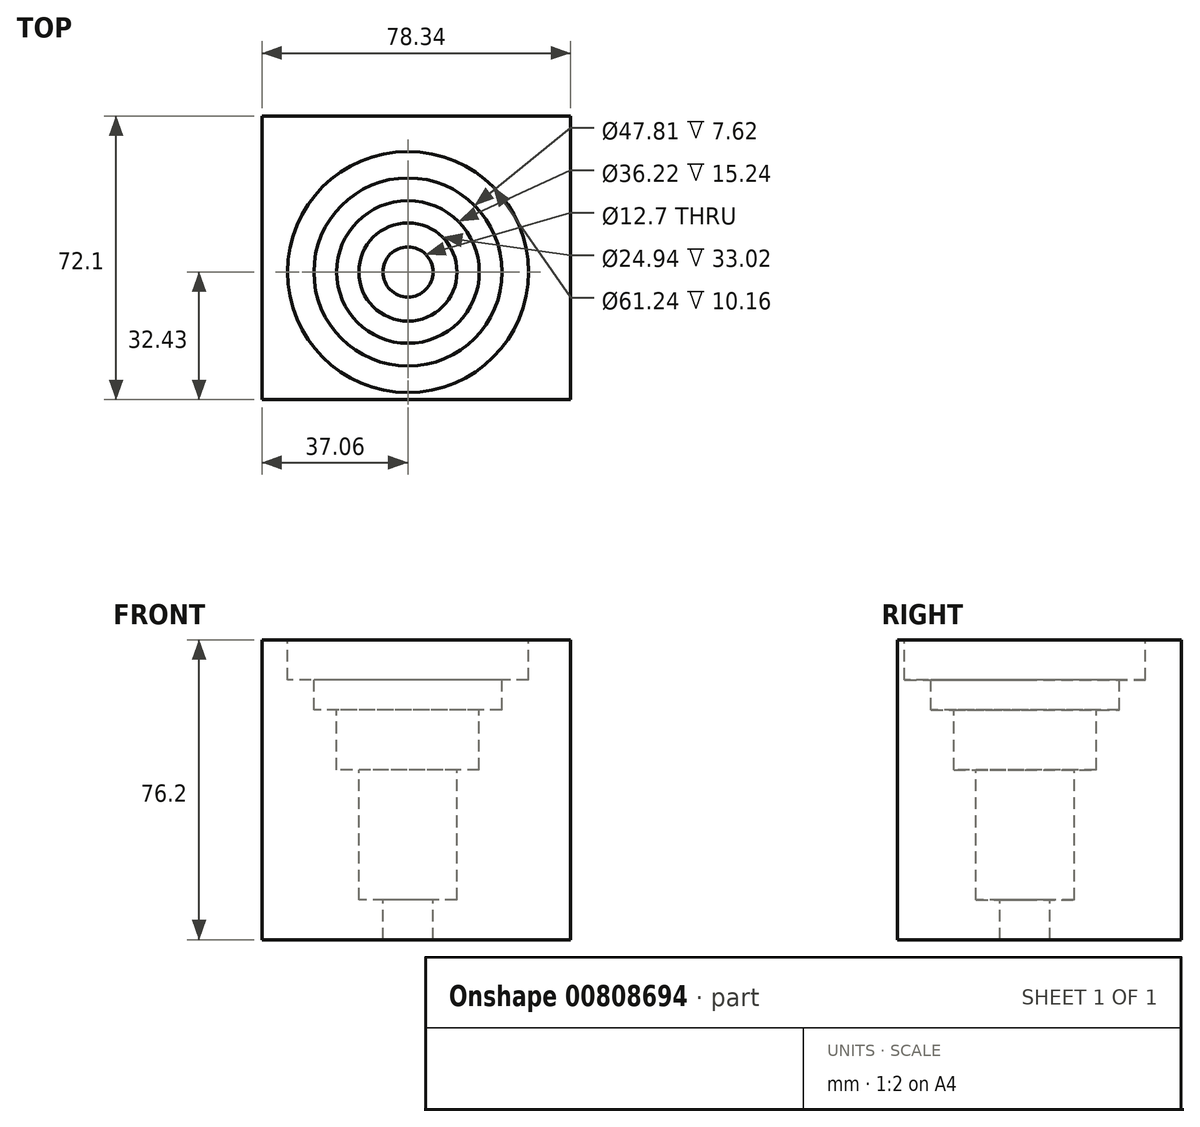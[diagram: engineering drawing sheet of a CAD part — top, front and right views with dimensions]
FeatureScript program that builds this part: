
annotation { "Feature Type Name" : "Feature", "Feature Type Description" : "" }
export const myFeature = defineFeature(function(context is Context, id is Id, definition is map)
    precondition{}
    {
        {
            var Q0;
            Q0=qCreatedBy(makeId("Top.planeOp"),FACE);
            var sketch = newSketch(context, id + "F0", { "sketchPlane" : qUnion([Q0])});
            skLineSegment(sketch, "E0.bottom", {"start": v(-37.06, -32.43) * mm, "end": v(41.28, -32.43) * mm});
            skLineSegment(sketch, "E0.top", {"start": v(-37.06, 39.67) * mm, "end": v(41.28, 39.67) * mm});
            skLineSegment(sketch, "E0.left", {"start": v(-37.06, -32.43) * mm, "end": v(-37.06, 39.67) * mm});
            skLineSegment(sketch, "E0.right", {"start": v(41.28, -32.43) * mm, "end": v(41.28, 39.67) * mm});
            skSolve(sketch);
        }
        {
            var Q0;
            Q0 = qSketchRegion(id + "F0", true);
            extrude(context, id + "F1", {"entities" : qUnion([Q0]), "depth" : 76.2 * mm, "offsetDistance" : 25.4 * mm});
        }
        {
            var Q0;
            Q0=makeQuery(id+"F1.opExtrude","CAP_FACE",FACE,{"disambiguationData":[OSD([sQuery(id+"F0.wireOp",EDGE,"E0.bottom"),sQuery(id+"F0.wireOp",EDGE,"E0.top"),sQuery(id+"F0.wireOp",EDGE,"E0.left"),sQuery(id+"F0.wireOp",EDGE,"E0.right")])],"isStart":false});
            var sketch = newSketch(context, id + "F2", { "sketchPlane" : qUnion([Q0])});
            skCircle(sketch, "E1", {"center": v(0, 0) * mm, "radius": 18.11 * mm});
            skSolve(sketch);
        }
        {
            var Q0;
            Q0 = qSketchRegion(id + "F2", true);
            extrude(context, id + "F3", {"entities" : qUnion([Q0]), "operationType" : NewBodyOperationType.REMOVE, "oppositeDirection" : true, "depth" : 33.02 * mm, "offsetDistance" : 25.4 * mm});
        }
        {
            var Q0;
            Q0=makeQuery(id+"F3.boolean.opBoolean","COPY",FACE,{"derivedFrom":makeQuery(id+"F3.opExtrude","CAP_FACE",FACE,{"disambiguationData":[OSD([sQuery(id+"F2.wireOp",EDGE,"E1")])],"isStart":false})});
            var sketch = newSketch(context, id + "F4", { "sketchPlane" : qUnion([Q0])});
            skCircle(sketch, "E2", {"center": v(0, 0) * mm, "radius": 6.35 * mm});
            skSolve(sketch);
        }
        {
            var Q0;
            Q0 = qSketchRegion(id + "F4", true);
            extrude(context, id + "F5", {"entities" : qUnion([Q0]), "operationType" : NewBodyOperationType.REMOVE, "oppositeDirection" : true, "depth" : 50.8 * mm, "offsetDistance" : 25.4 * mm});
        }
        {
            var Q0;
            Q0=makeQuery(id+"F3.boolean.opBoolean","COPY",FACE,{"derivedFrom":makeQuery(id+"F3.opExtrude","CAP_FACE",FACE,{"disambiguationData":[OSD([sQuery(id+"F2.wireOp",EDGE,"E1")])],"isStart":false})});
            var sketch = newSketch(context, id + "F6", { "sketchPlane" : qUnion([Q0])});
            skCircle(sketch, "E3", {"center": v(0, 0) * mm, "radius": 12.47 * mm});
            skSolve(sketch);
        }
        {
            var Q0;
            Q0=makeQuery(id+"F6.imprint","IMPRINT",FACE,{"disambiguationData":[TD([[makeQuery(id+"F6.imprint","IMPRINT",EDGE,{"derivedFrom":sQuery(id+"F6.wireOp",EDGE,"E3")}),1.0]])]});
            var Q1;
            Q1=sQuery(id+"F6.wireOp",EDGE,"E3");
            extrude(context, id + "F7", {"entities" : qUnion([Q0]), "operationType" : NewBodyOperationType.REMOVE, "surfaceEntities" : qUnion([Q1]), "oppositeDirection" : true, "depth" : 33.02 * mm, "offsetDistance" : 25.4 * mm});
        }
        {
            var Q0;
            Q0=makeQuery(id+"F1.opExtrude","CAP_FACE",FACE,{"disambiguationData":[OSD([sQuery(id+"F0.wireOp",EDGE,"E0.bottom"),sQuery(id+"F0.wireOp",EDGE,"E0.top"),sQuery(id+"F0.wireOp",EDGE,"E0.left"),sQuery(id+"F0.wireOp",EDGE,"E0.right")])],"isStart":false});
            var sketch = newSketch(context, id + "F8", { "sketchPlane" : qUnion([Q0])});
            skCircle(sketch, "E4", {"center": v(0, 0) * mm, "radius": 23.9 * mm});
            skSolve(sketch);
        }
        {
            var Q0;
            Q0 = qSketchRegion(id + "F8", true);
            extrude(context, id + "F9", {"entities" : qUnion([Q0]), "operationType" : NewBodyOperationType.REMOVE, "oppositeDirection" : true, "depth" : 17.78 * mm, "offsetDistance" : 25.4 * mm});
        }
        {
            var Q0;
            Q0=makeQuery(id+"F1.opExtrude","CAP_FACE",FACE,{"disambiguationData":[OSD([sQuery(id+"F0.wireOp",EDGE,"E0.bottom"),sQuery(id+"F0.wireOp",EDGE,"E0.top"),sQuery(id+"F0.wireOp",EDGE,"E0.left"),sQuery(id+"F0.wireOp",EDGE,"E0.right")])],"isStart":false});
            var sketch = newSketch(context, id + "F10", { "sketchPlane" : qUnion([Q0])});
            skCircle(sketch, "E5", {"center": v(0, 0) * mm, "radius": 30.62 * mm});
            skSolve(sketch);
        }
        {
            var Q0;
            Q0 = qSketchRegion(id + "F10", true);
            extrude(context, id + "F11", {"entities" : qUnion([Q0]), "operationType" : NewBodyOperationType.REMOVE, "oppositeDirection" : true, "depth" : 10.16 * mm, "offsetDistance" : 25.4 * mm});
        }
    });
